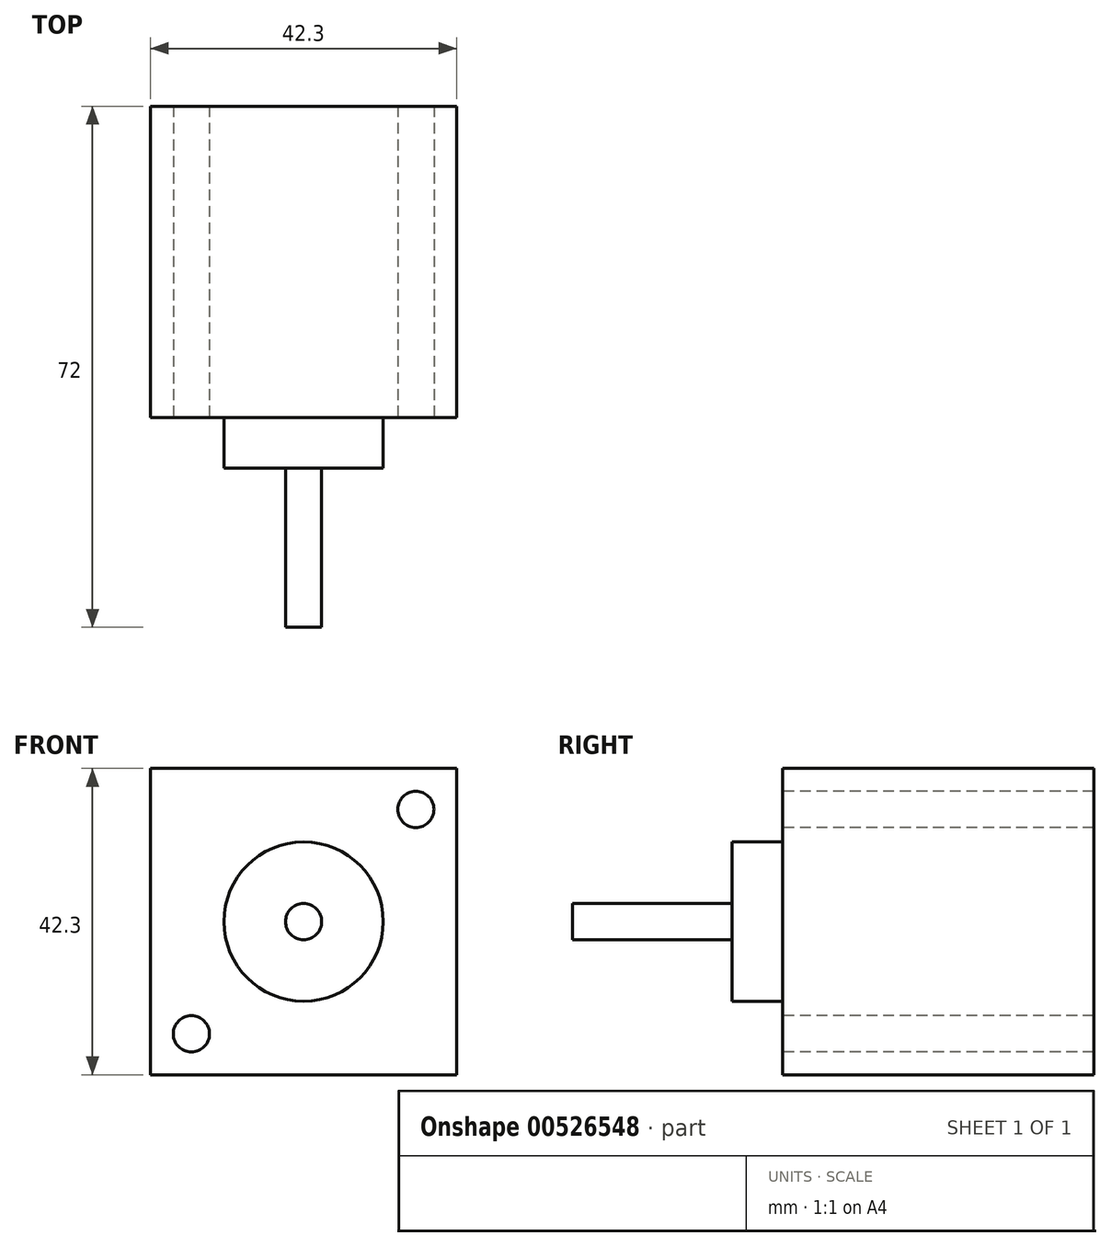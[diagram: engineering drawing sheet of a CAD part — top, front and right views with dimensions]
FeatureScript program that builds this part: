
annotation { "Feature Type Name" : "Feature", "Feature Type Description" : "" }
export const myFeature = defineFeature(function(context is Context, id is Id, definition is map)
    precondition{}
    {
        {
            var Q0;
            Q0=qCreatedBy(makeId("Front.planeOp"),FACE);
            var sketch = newSketch(context, id + "F0", { "sketchPlane" : qUnion([Q0])});
            skLineSegment(sketch, "E0.bottom", {"start": v(-21.15, 21.15) * mm, "end": v(21.15, 21.15) * mm});
            skLineSegment(sketch, "E0.top", {"start": v(-21.15, -21.15) * mm, "end": v(21.15, -21.15) * mm});
            skLineSegment(sketch, "E0.left", {"start": v(-21.15, 21.15) * mm, "end": v(-21.15, -21.15) * mm});
            skLineSegment(sketch, "E0.right", {"start": v(21.15, 21.15) * mm, "end": v(21.15, -21.15) * mm});
            skPoint(sketch, "E0.middle", {"position": v(0, 0) * mm});
            skCircle(sketch, "E1", {"center": v(-15.5, 15.5) * mm, "radius": 2.5 * mm});
            skCircle(sketch, "E2.MirrorC", {"center": v(15.5, 15.5) * mm, "radius": 2.5 * mm});
            skCircle(sketch, "E3.MirrorC", {"center": v(-15.5, -15.5) * mm, "radius": 2.5 * mm});
            skCircle(sketch, "E4.MirrorC", {"center": v(15.5, -15.5) * mm, "radius": 2.5 * mm});
            skCircle(sketch, "E5", {"center": v(0, 0) * mm, "radius": 2.5 * mm});
            skCircle(sketch, "E6", {"center": v(0, 0) * mm, "radius": 11 * mm});
            skSolve(sketch);
        }
        {
            var Q0;
            Q0=makeQuery(id+"F0.imprint","IMPRINT",FACE,{"disambiguationData":[TD([[makeQuery(id+"F0.imprint","IMPRINT",EDGE,{"derivedFrom":sQuery(id+"F0.wireOp",EDGE,"E1")}),1.0]])]});
            var Q1;
            Q1=makeQuery(id+"F0.imprint","IMPRINT",FACE,{"disambiguationData":[TD([[makeQuery(id+"F0.imprint","IMPRINT",EDGE,{"derivedFrom":sQuery(id+"F0.wireOp",EDGE,"E0.bottom")}),-1.0]])]});
            var Q2;
            Q2=makeQuery(id+"F0.imprint","IMPRINT",FACE,{"disambiguationData":[TD([[makeQuery(id+"F0.imprint","IMPRINT",EDGE,{"derivedFrom":sQuery(id+"F0.wireOp",EDGE,"E5")}),-1.0]])]});
            var Q3;
            Q3=makeQuery(id+"F0.imprint","IMPRINT",FACE,{"disambiguationData":[TD([[makeQuery(id+"F0.imprint","IMPRINT",EDGE,{"derivedFrom":sQuery(id+"F0.wireOp",EDGE,"E5")}),1.0]])]});
            var Q4;
            Q4=makeQuery(id+"F0.imprint","IMPRINT",FACE,{"disambiguationData":[TD([[makeQuery(id+"F0.imprint","IMPRINT",EDGE,{"derivedFrom":sQuery(id+"F0.wireOp",EDGE,"E2.MirrorC")}),-1.0]])]});
            var Q5;
            Q5=makeQuery(id+"F0.imprint","IMPRINT",FACE,{"disambiguationData":[TD([[makeQuery(id+"F0.imprint","IMPRINT",EDGE,{"derivedFrom":sQuery(id+"F0.wireOp",EDGE,"E3.MirrorC")}),-1.0]])]});
            var Q6;
            Q6=makeQuery(id+"F0.imprint","IMPRINT",FACE,{"disambiguationData":[TD([[makeQuery(id+"F0.imprint","IMPRINT",EDGE,{"derivedFrom":sQuery(id+"F0.wireOp",EDGE,"E4.MirrorC")}),1.0]])]});
            extrude(context, id + "F1", {"entities" : qUnion([Q0, Q1, Q2, Q3, Q4, Q5, Q6]), "oppositeDirection" : true, "depth" : 48 * mm, "offsetDistance" : 25 * mm});
        }
        {
            var Q0;
            Q0=makeQuery(id+"F0.imprint","IMPRINT",FACE,{"disambiguationData":[TD([[makeQuery(id+"F0.imprint","IMPRINT",EDGE,{"derivedFrom":sQuery(id+"F0.wireOp",EDGE,"E1")}),1.0]])]});
            var Q1;
            Q1=makeQuery(id+"F0.imprint","IMPRINT",FACE,{"disambiguationData":[TD([[makeQuery(id+"F0.imprint","IMPRINT",EDGE,{"derivedFrom":sQuery(id+"F0.wireOp",EDGE,"E2.MirrorC")}),-1.0]])]});
            var Q2;
            Q2=makeQuery(id+"F0.imprint","IMPRINT",FACE,{"disambiguationData":[TD([[makeQuery(id+"F0.imprint","IMPRINT",EDGE,{"derivedFrom":sQuery(id+"F0.wireOp",EDGE,"E4.MirrorC")}),1.0]])]});
            var Q3;
            Q3=makeQuery(id+"F0.imprint","IMPRINT",FACE,{"disambiguationData":[TD([[makeQuery(id+"F0.imprint","IMPRINT",EDGE,{"derivedFrom":sQuery(id+"F0.wireOp",EDGE,"E3.MirrorC")}),-1.0]])]});
            extrude(context, id + "F2", {"entities" : qUnion([Q0, Q1, Q2, Q3]), "operationType" : NewBodyOperationType.REMOVE, "oppositeDirection" : true, "depth" : 5 * mm, "offsetDistance" : 25 * mm});
        }
        {
            var Q0;
            Q0=makeQuery(id+"F0.imprint","IMPRINT",FACE,{"disambiguationData":[TD([[makeQuery(id+"F0.imprint","IMPRINT",EDGE,{"derivedFrom":sQuery(id+"F0.wireOp",EDGE,"E5")}),-1.0]])]});
            extrude(context, id + "F3", {"entities" : qUnion([Q0]), "operationType" : NewBodyOperationType.ADD, "depth" : 2 * mm, "offsetDistance" : 25 * mm});
        }
        {
            var Q0;
            Q0=makeQuery(id+"F0.imprint","IMPRINT",FACE,{"disambiguationData":[TD([[makeQuery(id+"F0.imprint","IMPRINT",EDGE,{"derivedFrom":sQuery(id+"F0.wireOp",EDGE,"E5")}),1.0]])]});
            extrude(context, id + "F4", {"entities" : qUnion([Q0]), "operationType" : NewBodyOperationType.ADD, "depth" : 24 * mm, "offsetDistance" : 25 * mm});
        }
    });
